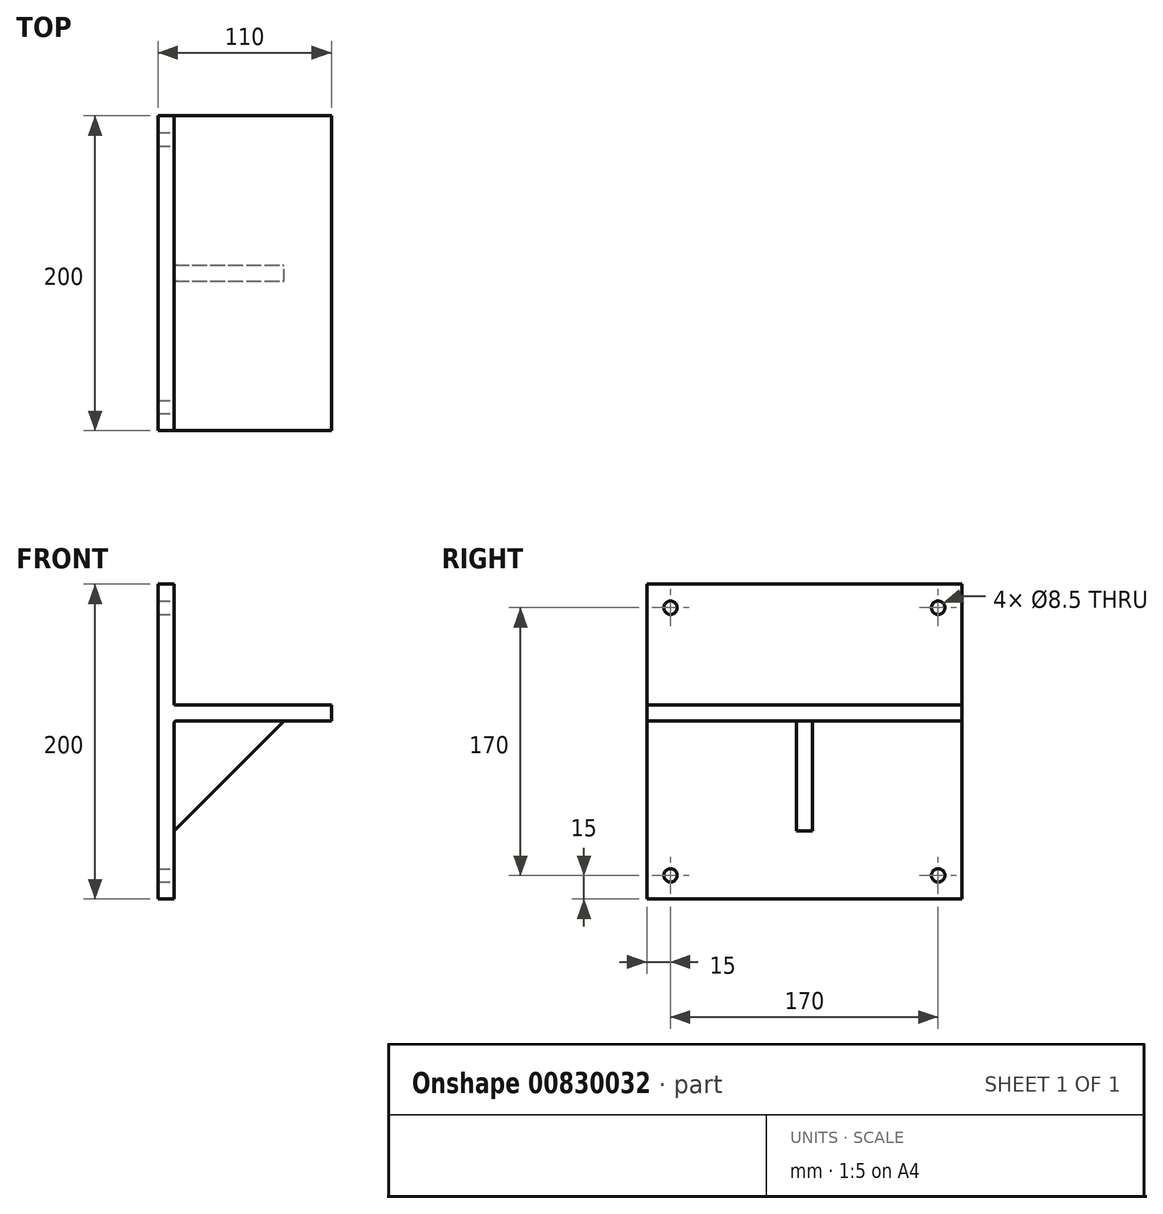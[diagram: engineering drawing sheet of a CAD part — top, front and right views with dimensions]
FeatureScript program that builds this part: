
annotation { "Feature Type Name" : "Feature", "Feature Type Description" : "" }
export const myFeature = defineFeature(function(context is Context, id is Id, definition is map)
    precondition{}
    {
        {
            var Q0;
            Q0=qCreatedBy(makeId("Front.planeOp"),FACE);
            var sketch = newSketch(context, id + "F0", { "sketchPlane" : qUnion([Q0])});
            skLineSegment(sketch, "E0.bottom", {"start": v(-27.58, 100) * mm, "end": v(-17.58, 100) * mm});
            skLineSegment(sketch, "E0.top", {"start": v(-27.58, -100) * mm, "end": v(-17.58, -100) * mm});
            skLineSegment(sketch, "E0.left", {"start": v(-27.58, 100) * mm, "end": v(-27.58, -100) * mm});
            skLineSegment(sketch, "E0.right", {"start": v(-17.58, 100) * mm, "end": v(-17.58, -100) * mm});
            skLineSegment(sketch, "E1.bottom", {"start": v(-27.58, 23.2) * mm, "end": v(82.42, 23.2) * mm});
            skLineSegment(sketch, "E1.top", {"start": v(-27.58, 13.2) * mm, "end": v(82.42, 13.2) * mm});
            skLineSegment(sketch, "E1.left", {"start": v(-27.58, 23.2) * mm, "end": v(-27.58, 13.2) * mm});
            skLineSegment(sketch, "E1.right", {"start": v(82.42, 23.2) * mm, "end": v(82.42, 13.2) * mm});
            skSolve(sketch);
        }
        {
            var Q0;
            Q0 = qSketchRegion(id + "F0", true);
            extrude(context, id + "F1", {"entities" : qUnion([Q0]), "endBound" : BoundingType.SYMMETRIC, "depth" : 200 * mm, "offsetDistance" : 25 * mm});
        }
        {
            var Q0;
            Q0=qCreatedBy(makeId("Front.planeOp"),FACE);
            var sketch = newSketch(context, id + "F2", { "sketchPlane" : qUnion([Q0])});
            skLineSegment(sketch, "E2", {"start": v(-17.58, -56.8) * mm, "end": v(52.42, 13.2) * mm});
            skLineSegment(sketch, "E3", {"start": v(-17.58, -56.8) * mm, "end": v(-17.58, 13.2) * mm});
            skLineSegment(sketch, "E4", {"start": v(-17.58, 13.2) * mm, "end": v(52.42, 13.2) * mm});
            skSolve(sketch);
        }
        {
            var Q0;
            Q0 = qSketchRegion(id + "F2", true);
            extrude(context, id + "F3", {"entities" : qUnion([Q0]), "operationType" : NewBodyOperationType.ADD, "endBound" : BoundingType.SYMMETRIC, "depth" : 10 * mm, "offsetDistance" : 25 * mm});
        }
        {
            var Q0;
            Q0=makeQuery(id+"F3.opExtrude","CAP_EDGE",EDGE,{"disambiguationData":[OSD([sQuery(id+"F2.wireOp",EDGE,"E4")])],"isStart":false});
            var Q1;
            Q1=makeQuery(id+"F3.opExtrude","CAP_EDGE",EDGE,{"disambiguationData":[OSD([sQuery(id+"F2.wireOp",EDGE,"E3")])],"isStart":false});
            var Q2;
            {var subQ0=sQuery(id+"F0.wireOp",EDGE,"E1.top");var subQ1=sQuery(id+"F0.wireOp",EDGE,"E0.right");Q2=makeQuery(id+"F3.boolean.opBoolean","SPLIT",EDGE,{"disambiguationData":[TD([makeQuery(id+"F3.opExtrude","CAP_FACE",FACE,{"disambiguationData":[OSD([sQuery(id+"F2.wireOp",EDGE,"E2"),sQuery(id+"F2.wireOp",EDGE,"E3"),sQuery(id+"F2.wireOp",EDGE,"E4")])],"isStart":false})])],"derivedFrom":makeQuery(id+"F1.opExtrude","SWEPT_EDGE",EDGE,{"disambiguationData":[OSD([subQ1,subQ0])]})});}
            var Q3;
            {var subQ0=sQuery(id+"F0.wireOp",EDGE,"E1.top");var subQ1=sQuery(id+"F0.wireOp",EDGE,"E0.right");Q3=makeQuery(id+"F3.boolean.opBoolean","SPLIT",EDGE,{"disambiguationData":[TD([makeQuery(id+"F3.opExtrude","CAP_FACE",FACE,{"disambiguationData":[OSD([sQuery(id+"F2.wireOp",EDGE,"E2"),sQuery(id+"F2.wireOp",EDGE,"E3"),sQuery(id+"F2.wireOp",EDGE,"E4")])],"isStart":true})])],"derivedFrom":makeQuery(id+"F1.opExtrude","SWEPT_EDGE",EDGE,{"disambiguationData":[OSD([subQ1,subQ0])]})});}
            var Q4;
            Q4=makeQuery(id+"F3.opExtrude","CAP_EDGE",EDGE,{"disambiguationData":[OSD([sQuery(id+"F2.wireOp",EDGE,"E3")])],"isStart":true});
            var Q5;
            Q5=makeQuery(id+"F3.opExtrude","CAP_EDGE",EDGE,{"disambiguationData":[OSD([sQuery(id+"F2.wireOp",EDGE,"E4")])],"isStart":true});
            fillet(context, id + "F4", {"entities" : qUnion([Q0, Q1, Q2, Q3, Q4, Q5]), "radius" : 2 * mm, "tangentPropagation" : true, "allowEdgeOverflow" : false});
        }
        {
            var Q0;
            {var subQ0=sQuery(id+"F0.wireOp",EDGE,"E0.right");Q0=makeQuery(id+"F1.opExtrude","SWEPT_FACE",FACE,{"disambiguationData":[OSD([subQ0]),TDD([makeQuery(id+"F0.imprint","IMPRINT",EDGE,{"disambiguationData":[TD([[makeQuery(id+"F0.imprint","INTERSECT",VERTEX,{"derivedFrom":[sQuery(id+"F0.wireOp",EDGE,"E0.bottom"),subQ0]}),-1.0]])],"derivedFrom":subQ0})])]});}
            var sketch = newSketch(context, id + "F5", { "sketchPlane" : qUnion([Q0])});
            skPoint(sketch, "E5", {"position": v(-85, 85) * mm});
            skPoint(sketch, "E6.MirrorP", {"position": v(85, 85) * mm});
            skPoint(sketch, "E7.MirrorP", {"position": v(85, -85) * mm});
            skPoint(sketch, "E8.MirrorP", {"position": v(-85, -85) * mm});
            skSolve(sketch);
        }
        {
            var Q0;
            Q0=sQuery(id+"F5.wireOp",VERTEX,"E5");
            var Q1;
            Q1=sQuery(id+"F5.wireOp",VERTEX,"E6.MirrorP");
            var Q2;
            Q2=sQuery(id+"F5.wireOp",VERTEX,"E7.MirrorP");
            var Q3;
            Q3=sQuery(id+"F5.wireOp",VERTEX,"E8.MirrorP");
            var Q4;
            Q4=makeQuery(id+"F1.opExtrude","SWEPT_BODY",BODY,{"disambiguationData":[OSD([sQuery(id+"F0.wireOp",EDGE,"E0.bottom"),sQuery(id+"F0.wireOp",EDGE,"E0.top"),sQuery(id+"F0.wireOp",EDGE,"E0.left"),sQuery(id+"F0.wireOp",EDGE,"E0.right"),sQuery(id+"F0.wireOp",EDGE,"E1.bottom"),sQuery(id+"F0.wireOp",EDGE,"E1.top"),sQuery(id+"F0.wireOp",EDGE,"E1.left"),sQuery(id+"F0.wireOp",EDGE,"E1.right")])]});
            hole(context, id + "F6", {"style" : HoleStyle.SIMPLE, "endStyle" : HoleEndStyle.THROUGH, "holeDiameter" : 8.5 * mm, "majorDiameter" : 5 * mm, "isTappedThrough" : true, "tappedDepth" : 12 * mm, "tapClearance" : 3, "locations" : qUnion([Q0, Q1, Q2, Q3]), "scope" : qUnion([Q4])});
        }
    });
